FCSTD DOCUMENT  (FreeCAD 1.0R39109 (Git))
Label: outline
License: All rights reserved
LicenseURL: https://en.wikipedia.org/wiki/All_rights_reserved
objects: Sketcher::SketchObject×1
note: 2 computed .brp shape members not serialized (recipe doc carries the construction recipe); baked Part::Feature solids carry a one-line shape summary decoded from their .brp

FEATURE [Sketcher::SketchObject] Sketch
  ArcFitTolerance = 1e-06
  FullyConstrained = true
  MakeInternals = false
  sketch-geometry (8):
    g0: LineSegment StartX=-7.5 StartY=-3.5 StartZ=0 EndX=-4.3 EndY=-3.5 EndZ=0
    g1: LineSegment StartX=-4.3 StartY=-3.5 StartZ=0 EndX=-4.3 EndY=0 EndZ=0
    g2: LineSegment StartX=-4.3 StartY=0 StartZ=0 EndX=4.3 EndY=0 EndZ=0
    g3: LineSegment StartX=4.3 StartY=0 StartZ=0 EndX=4.3 EndY=-3.5 EndZ=0
    g4: LineSegment StartX=4.3 StartY=-3.5 StartZ=0 EndX=7.5 EndY=-3.5 EndZ=0
    g5: LineSegment StartX=7.5 StartY=28.5 StartZ=0 EndX=-7.5 EndY=28.5 EndZ=0
    g6: LineSegment StartX=7.5 StartY=28.5 StartZ=0 EndX=7.5 EndY=-3.5 EndZ=0
    g7: LineSegment StartX=-7.5 StartY=28.5 StartZ=0 EndX=-7.5 EndY=-3.5 EndZ=0
  constraints (23):
    c: Horizontal(g0)
    c: Coincident(g0,g1)
    c: Vertical(g1)
    c: Coincident(g1,g2)
    c: Coincident(g2,g3)
    c: Vertical(g3)
    c: Coincident(g3,g4)
    c: Horizontal(g4)
    c: Horizontal(g5)
    c: Equal(g0,g4)
    c: Horizontal(g0,g3)
    c: Symmetric(g1,g2,g-2)
    c: Horizontal(g2,g-1)
    c: DistanceY(g1,g1) = 3.5
    c: DistanceX(g2,g2) = 8.6
    c: DistanceX(g5,g5) = 15
    c: DistanceY(g0,g5) = 32
    c: Coincident(g6,g5)
    c: Coincident(g6,g4)
    c: Vertical(g6)
    c: Coincident(g7,g5)
    c: Coincident(g7,g0)
    c: Vertical(g7)
